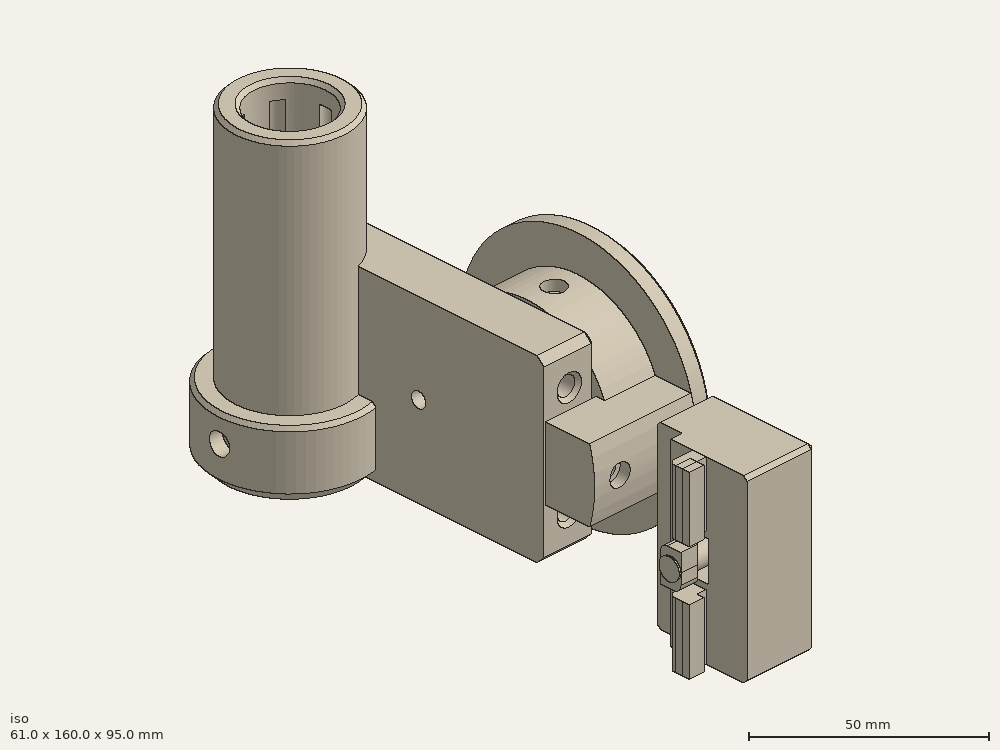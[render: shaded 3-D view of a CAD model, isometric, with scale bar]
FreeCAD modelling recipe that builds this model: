
FCSTD DOCUMENT  (FreeCAD 0.18R16146 (Git))
Label: mini-spoll-holder
License: All rights reserved
LicenseURL: http://en.wikipedia.org/wiki/All_rights_reserved
objects: Part::Cylinder×42, Part::Cut×37, Part::Box×20, Part::Chamfer×17, Part::MultiFuse×17, Part::Feature×11, Part::MultiCommon×1, Part::Fillet×1
note: 146 computed .brp shape members not serialized (recipe doc carries the construction recipe); baked Part::Feature solids carry a one-line shape summary decoded from their .brp

FEATURE [Part::Cylinder] Cylinder
  Angle = 360
  AttacherType = Attacher::AttachEngine3D
  Height = 47
  Placement = pos=(9.99127,-50,25.0035) rot=(0,1,0;1.57045rad)
  Radius = 9.65
FEATURE [Part::Box] Box003  label="Cube003"
  AttacherType = Attacher::AttachEngine3D
  Height = 50
  Length = 20
  Placement = pos=(0,-70,0) rot=(0,0,1;0rad)
  Width = 95
FEATURE [Part::Cylinder] Cylinder001
  Angle = 360
  AttacherType = Attacher::AttachEngine3D
  Height = 110
  Placement = pos=(12.5,5.00349,9.99825) rot=(1,0,0;1.57045rad)
  Radius = 2.6
FEATURE [Part::Cylinder] Cylinder002
  Angle = 360
  AttacherType = Attacher::AttachEngine3D
  Height = 110
  Placement = pos=(12.5,5.01396,39.9983) rot=(1,0,0;1.57045rad)
  Radius = 2.6
FEATURE [Part::Box] Box004  label="Cube004"
  AttacherType = Attacher::AttachEngine3D
  Height = 50
  Length = 5
  Placement = pos=(0,-70,0) rot=(0,0,1;0rad)
  Width = 70
FEATURE [Part::Chamfer] Chamfer
  Base = -> Box004
  Edges = 1 edges r=1.5: [Edge7]
FEATURE [Part::Cylinder] Cylinder003
  Angle = 360
  AttacherType = Attacher::AttachEngine3D
  Height = 27
  Placement = pos=(-3,15,-0.0010472) rot=(0,1,0;1.57045rad)
  Radius = 2.6
FEATURE [Part::Cylinder] Cylinder004
  Angle = 360
  AttacherType = Attacher::AttachEngine3D
  Height = 6
  Placement = pos=(15,15,0.00523599) rot=(0,1,0;1.57045rad)
  Radius = 6.5
FEATURE [Part::Cut] Cut
  Base = -> Box003
  Tool = -> Chamfer
FEATURE [Part::Box] Box005  label="Cube005"
  AttacherType = Attacher::AttachEngine3D
  Height = 50
  Length = 3.5
  Placement = pos=(0,19.5,0) rot=(0,0,1;0rad)
  Width = 15
FEATURE [Part::Cut] Cut001
  Base = -> Cut
  Tool = -> Box005
FEATURE [Part::Box] Box006  label="Cube006"
  AttacherType = Attacher::AttachEngine3D
  Height = 5
  Length = 2
  Placement = pos=(-2,11.9,0) rot=(0,0,1;0rad)
  Width = 6.2
FEATURE [Part::Box] Box007  label="Cube007"
  AttacherType = Attacher::AttachEngine3D
  Height = 5
  Length = 2
  Placement = pos=(-2,11.9,45) rot=(0,0,1;0rad)
  Width = 6.2
FEATURE [Part::Box] Box008  label="Cube008"
  AttacherType = Attacher::AttachEngine3D
  Height = 20
  Length = 2
  Placement = pos=(-2,11.9,15) rot=(0,0,1;0rad)
  Width = 6.2
FEATURE [Part::MultiFuse] Fusion002
  Shapes = -> [Box007,Box008,Box006,Cut001]
FEATURE [Part::MultiFuse] Fusion003
  Placement = pos=(0,0,10) rot=(0,0,1;0rad)
  Shapes = -> [Cylinder003,Cylinder004]
FEATURE [Part::Feature] Fusion003001  label="Fusion004"
  Placement = pos=(0,0,40) rot=(0,0,1;0rad)
  shape: bbox 27 x 13 x 13 mm, 7 faces (baked)
FEATURE [Part::MultiFuse] Fusion003002
  Shapes = -> [Fusion003001,Fusion003]
FEATURE [Part::Cut] Cut002
  Base = -> Fusion002
  Tool = -> Fusion003002
FEATURE [Part::Cylinder] Cylinder005
  Angle = 360
  AttacherType = Attacher::AttachEngine3D
  Height = 47
  Placement = pos=(9.99127,-50,25.0035) rot=(0,1,0;1.57045rad)
  Radius = 8.65
FEATURE [Part::Cut] Cut003
  Base = -> Cylinder
  Tool = -> Cylinder005
FEATURE [Part::Cut] Cut004
  Base = -> Cut002
  Tool = -> Cut003
FEATURE [Part::Chamfer] Chamfer001
  Base = -> Cut004
  Edges = 4 edges r=2: [Edge22,Edge24,Edge36,Edge38]
FEATURE [Part::Cylinder] Cylinder006
  Angle = 360
  AttacherType = Attacher::AttachEngine3D
  Height = 20
  Placement = pos=(24.9913,-50,25.0087) rot=(0,1,0;1.57045rad)
  Radius = 9.65
FEATURE [Part::Cylinder] Cylinder008
  Angle = 360
  AttacherType = Attacher::AttachEngine3D
  Height = 5
  Placement = pos=(39.9913,-50,25.014) rot=(0,1,0;1.57045rad)
  Radius = 35
FEATURE [Part::Cylinder] Cylinder009
  Angle = 360
  AttacherType = Attacher::AttachEngine3D
  Height = 30
  Placement = pos=(9.99127,-50,25.0035) rot=(0,1,0;1.57045rad)
  Radius = 35
FEATURE [Part::Box] Box010  label="Cube010"
  AttacherType = Attacher::AttachEngine3D
  Height = 89
  Length = 48
  Placement = pos=(0,-70.5,-13) rot=(0,0,1;0rad)
  Width = 60
FEATURE [Part::Cylinder] Cylinder007
  Angle = 360
  AttacherType = Attacher::AttachEngine3D
  Height = 20
  Placement = pos=(24.9913,-50,25.0087) rot=(0,1,0;1.57045rad)
  Radius = 25
FEATURE [Part::Box] Box011  label="Cube011"
  AttacherType = Attacher::AttachEngine3D
  Height = 20
  Length = 32
  Placement = pos=(10,-90,15) rot=(0,0,1;0rad)
  Width = 20
FEATURE [Part::Cut] Cut005
  Base = -> Cylinder009
  Tool = -> Box010
FEATURE [Part::MultiCommon] Common
  Shapes = -> [Box011,Cut005]
FEATURE [Part::MultiFuse] Fusion003003
  Shapes = -> [Cylinder007,Common,Cylinder008]
FEATURE [Part::Cut] Cut006
  Base = -> Fusion003003
  Placement = pos=(-5,0,0) rot=(0,0,1;0rad)
  Tool = -> Cylinder006
FEATURE [Part::Cylinder] Cylinder010
  Angle = 360
  AttacherType = Attacher::AttachEngine3D
  Height = 37
  Placement = pos=(12.5,-96.5087,24.9977) rot=(-1,0,0;1.57045rad)
  Radius = 1.65
FEATURE [Part::Cylinder] Cylinder011
  Angle = 360
  AttacherType = Attacher::AttachEngine3D
  Height = 37
  Placement = pos=(12.5,-90.0087,25) rot=(-1,0,0;1.57045rad)
  Radius = 1.65
FEATURE [Part::Cylinder] Cylinder012
  Angle = 360
  AttacherType = Attacher::AttachEngine3D
  Height = 37
  Placement = pos=(12.5,-119.009,24.9899) rot=(-1,0,0;1.57045rad)
  Radius = 3
FEATURE [Part::Cylinder] Cylinder013
  Angle = 360
  AttacherType = Attacher::AttachEngine3D
  Height = 37
  Placement = pos=(12.5,-100.009,24.9965) rot=(-1,0,0;1.57045rad)
  Radius = 2.1
FEATURE [Part::Cut] Cut007
  Base = -> Chamfer001
  Tool = -> Cylinder010
FEATURE [Part::Cut] Cut008
  Base = -> Cut007
  Tool = -> Cylinder013
FEATURE [Part::Cut] Cut009
  Base = -> Cut006
  Tool = -> Cylinder011
FEATURE [Part::Cut] Cut010
  Base = -> Cut009
  Tool = -> Cylinder012
FEATURE [Part::Cylinder] Cylinder014
  Angle = 360
  AttacherType = Attacher::AttachEngine3D
  Height = 11
  Placement = pos=(28,-50,47) rot=(0,0,1;0rad)
  Radius = 3
FEATURE [Part::Cylinder] Cylinder015
  Angle = 360
  AttacherType = Attacher::AttachEngine3D
  Height = 59
  Placement = pos=(28,-50,0) rot=(0,0,1;0rad)
  Radius = 1.65
FEATURE [Part::Cut] Cut011
  Base = -> Cut010
  Tool = -> Cylinder015
FEATURE [Part::Cylinder] Cylinder016
  Angle = 360
  AttacherType = Attacher::AttachEngine3D
  Height = 10
  Placement = pos=(28,-50,-7) rot=(0,0,1;0rad)
  Radius = 3
FEATURE [Part::Cylinder] Cylinder017
  Angle = 360
  AttacherType = Attacher::AttachEngine3D
  Height = 8
  Placement = pos=(34.9913,-33,25.0122) rot=(0,1,0;1.57045rad)
  Radius = 3
FEATURE [Part::Cylinder] Cylinder018
  Angle = 360
  AttacherType = Attacher::AttachEngine3D
  Height = 61
  Placement = pos=(3.99127,-33,25.0014) rot=(0,1,0;1.57045rad)
  Radius = 1.65
FEATURE [Part::Cylinder] Cylinder019
  Angle = 360
  AttacherType = Attacher::AttachEngine3D
  Height = 61
  Placement = pos=(3.99127,-33,25.0014) rot=(0,1,0;1.57045rad)
  Radius = 1.65
FEATURE [Part::Cut] Cut014
  Base = -> Cut008
  Tool = -> Cylinder018
FEATURE [Part::Cylinder] Cylinder020
  Angle = 360
  AttacherType = Attacher::AttachEngine3D
  Height = 7
  Placement = pos=(3.99127,-33,25.0014) rot=(0,1,0;1.57045rad)
  Radius = 2.1
FEATURE [Part::Cut] Cut016
  Base = -> Cut014
  Tool = -> Cylinder020
FEATURE [Part::Cylinder] Cylinder021
  Angle = 360
  AttacherType = Attacher::AttachEngine3D
  Height = 110
  Placement = pos=(12.5,5.00349,9.99825) rot=(1,0,0;1.57045rad)
  Radius = 2.6
FEATURE [Part::Cylinder] Cylinder022
  Angle = 360
  AttacherType = Attacher::AttachEngine3D
  Height = 110
  Placement = pos=(12.5,5.01396,39.9983) rot=(1,0,0;1.57045rad)
  Radius = 2.6
FEATURE [Part::MultiFuse] Fusion003004
  Shapes = -> [Cylinder001,Cylinder002]
FEATURE [Part::MultiFuse] Fusion003005
  Placement = pos=(0,-20,0) rot=(0,0,1;0rad)
  Shapes = -> [Cylinder022,Cylinder021]
FEATURE [Part::Cut] Cut018
  Base = -> Cut016
  Tool = -> Fusion003004
FEATURE [Part::Box] Box012  label="Cube012"
  AttacherType = Attacher::AttachEngine3D
  Height = 50
  Length = 20
  Placement = pos=(0,-135,0) rot=(0,0,1;0rad)
  Width = 30
FEATURE [Part::Cut] Cut019
  Base = -> Box012
  Tool = -> Fusion003005
FEATURE [Part::Box] Box013  label="Cube013"
  AttacherType = Attacher::AttachEngine3D
  Height = 50
  Length = 7
  Placement = pos=(-7,-123,0) rot=(0,0,1;0rad)
  Width = 4
FEATURE [Part::Box] Box014  label="Cube014"
  AttacherType = Attacher::AttachEngine3D
  Height = 50
  Length = 4.3
  Placement = pos=(-7,-125,0) rot=(0,0,1;0rad)
  Width = 4
FEATURE [Part::Chamfer] Chamfer005
  Base = -> Cut019
  Edges = 8 edges r=1: [Edge5,Edge6,Edge7,Edge8,Edge9,Edge10,Edge11,Edge14]
FEATURE [Part::Chamfer] Chamfer006
  Base = -> Cut018
  Edges = 8 edges r=1: [Edge4,Edge18,Edge21,Edge22,Edge23,Edge24,Edge25,Edge26]
FEATURE [Part::Box] Box015  label="Cube015"
  AttacherType = Attacher::AttachEngine3D
  Height = 50
  Length = 3.5
  Placement = pos=(0,-112.5,0) rot=(0,0,1;0rad)
  Width = 7.5
FEATURE [Part::Cut] Cut020
  Base = -> Chamfer005
  Tool = -> Box015
FEATURE [Part::Box] Box016  label="Cube016"
  AttacherType = Attacher::AttachEngine3D
  Height = 14
  Length = 20
  Placement = pos=(-12,-125,18) rot=(0,0,1;0rad)
  Width = 10
FEATURE [Part::Box] Box017  label="Cube017"
  AttacherType = Attacher::AttachEngine3D
  Height = 11
  Length = 20
  Placement = pos=(0,-123.5,19.5) rot=(0,0,1;0rad)
  Width = 7
FEATURE [Part::Cylinder] Cylinder023
  Angle = 360
  AttacherType = Attacher::AttachEngine3D
  Height = 10
  Placement = pos=(12.9913,-120,25.0045) rot=(0,1,0;1.57045rad)
  Radius = 8
FEATURE [Part::Cut] Cut021
  Base = -> Cut020
  Tool = -> Box017
FEATURE [Part::Cut] Cut022
  Base = -> Cut021
  Tool = -> Cylinder023
FEATURE [Part::Chamfer] Chamfer007
  Base = -> Cut022
  Edges = 2 edges r=0.4: [Edge28,Edge32]
FEATURE [Part::Chamfer] Chamfer008
  Base = -> Chamfer007
  Edges = 1 edges r=1: [Edge46]
FEATURE [Part::Box] Box019  label="Cube019"
  AttacherType = Attacher::AttachEngine3D
  Height = 10
  Length = 5
  Placement = pos=(-7.5,-123,20) rot=(0,0,1;0rad)
  Width = 6
FEATURE [Part::Cylinder] Cylinder024
  Angle = 360
  AttacherType = Attacher::AttachEngine3D
  Height = 27
  Placement = pos=(-8.00873,-120,24.9972) rot=(0,1,0;1.57045rad)
  Radius = 3
FEATURE [Part::Fillet] Fillet
  Base = -> Box019
  Edges = 2 edges r=2: [Edge9,Edge12]
FEATURE [Part::Box] Box020  label="Cube020"
  AttacherType = Attacher::AttachEngine3D
  Height = 7
  Length = 7
  Placement = pos=(15,-121,21.5) rot=(0,0,1;0rad)
  Width = 2
FEATURE [Part::Cylinder] Cylinder025
  Angle = 360
  AttacherType = Attacher::AttachEngine3D
  Height = 7
  Placement = pos=(12.9913,-120,25.0045) rot=(0,1,0;1.57045rad)
  Radius = 7
FEATURE [Part::MultiFuse] Fusion003009
  Shapes = -> [Cylinder025,Fillet,Cylinder024]
FEATURE [Part::Chamfer] Chamfer012
  Base = -> Chamfer006
  Edges = 2 edges r=1: [Edge75,Edge77]
FEATURE [Part::Cylinder] Cylinder026
  Angle = 360
  AttacherType = Attacher::AttachEngine3D
  Height = 37
  Placement = pos=(-6e-15,-50,25) rot=(0,1,0;1.5708rad)
  Radius = 9.6
FEATURE [Part::Cylinder] Cylinder027
  Angle = 360
  AttacherType = Attacher::AttachEngine3D
  Height = 37
  Placement = pos=(-6e-15,-50,25) rot=(0,1,0;1.5708rad)
  Radius = 8.15
FEATURE [Part::Cut] Cut026
  Base = -> Cylinder026
  Placement = pos=(10,0,0) rot=(0,0,1;0rad)
  Tool = -> Cylinder027
FEATURE [Part::Cut] Cut027
  Base = -> Chamfer012
  Tool = -> Cut026
FEATURE [Part::Chamfer] Chamfer013  label="spool-top"
  Base = -> Cut027
  Edges = 2 edges r=1: [Edge49,Edge138]
FEATURE [Part::Cut] Cut028
  Base = -> Cut011
  Tool = -> Cylinder019
FEATURE [Part::Cut] Cut029
  Base = -> Cut028
  Tool = -> Cylinder017
FEATURE [Part::Cylinder] Cylinder028
  Angle = 360
  AttacherType = Attacher::AttachEngine3D
  Height = 11
  Placement = pos=(28,-50,40) rot=(0,0,1;0rad)
  Radius = 2.1
FEATURE [Part::Cylinder] Cylinder029
  Angle = 360
  AttacherType = Attacher::AttachEngine3D
  Height = 10
  Placement = pos=(28,-50,0) rot=(0,0,1;0rad)
  Radius = 2.1
FEATURE [Part::Cut] Cut030
  Base = -> Cut029
  Tool = -> Cylinder029
FEATURE [Part::Cut] Cut031
  Base = -> Cut030
  Tool = -> Cylinder028
FEATURE [Part::Cut] Cut032
  Base = -> Cut031
  Tool = -> Cylinder014
FEATURE [Part::Cut] Cut033
  Base = -> Cut032
  Tool = -> Cylinder016
FEATURE [Part::Chamfer] Chamfer014
  Base = -> Cut033
  Edges = 2 edges r=1: [Edge3,Edge4]
FEATURE [Part::Chamfer] Chamfer015  label="spool-side"
  Base = -> Chamfer014
  Edges = 1 edges r=0.4: [Edge3]
FEATURE [Part::Cut] Cut034
  Base = -> Fusion003009
  Tool = -> Box020
FEATURE [Part::Chamfer] Chamfer016  label="lock"
  Base = -> Cut034
  Edges = 5 edges r=0.4: [Edge1,Edge4,Edge5,Edge6,Edge7]
FEATURE [Part::Chamfer] Chamfer017
  Base = -> Box013
  Edges = 1 edges r=1: [Edge3]
FEATURE [Part::MultiFuse] Fusion
  Shapes = -> [Chamfer017,Box014]
FEATURE [Part::Cut] Cut035
  Base = -> Fusion
  Tool = -> Box016
FEATURE [Part::MultiFuse] Fusion003010
  Shapes = -> [Chamfer008,Cut035]
FEATURE [Part::Chamfer] Chamfer018  label="spool-bottom"
  Base = -> Fusion003010
  Edges = 2 edges r=1: [Edge77,Edge78]
FEATURE [Part::Cylinder] Cylinder035007  label="Cylinder042"
  Angle = 360
  AttacherType = Attacher::AttachEngine3D
  Height = 101
  Placement = pos=(0,0,-4) rot=(0,0,1;0rad)
  Radius = 10.5
FEATURE [Part::Cylinder] Cylinder035008  label="Cylinder043"
  Angle = 360
  AttacherType = Attacher::AttachEngine3D
  Height = 85
  Radius = 16
FEATURE [Part::Cylinder] Cylinder035009  label="Cylinder044"
  Angle = 360
  AttacherType = Attacher::AttachEngine3D
  Height = 10
  Placement = pos=(0,11.75,0) rot=(0,0,1;0rad)
  Radius = 2.25
FEATURE [Part::Feature] Cylinder035009001  label="Cylinder045"
  Placement = pos=(0,0,0) rot=(0,0,1;5.23599rad)
  shape: bbox 4.5 x 4.5 x 10 mm, 3 faces (baked)
FEATURE [Part::Feature] Cylinder035009002  label="Cylinder046"
  Placement = pos=(0,0,0) rot=(0,0,1;4.18879rad)
  shape: bbox 4.5 x 4.5 x 10 mm, 3 faces (baked)
FEATURE [Part::Feature] Cylinder035009003  label="Cylinder047"
  Placement = pos=(0,0,0) rot=(0,0,-1;3.14159rad)
  shape: bbox 4.5 x 4.5 x 10 mm, 3 faces (baked)
FEATURE [Part::Feature] Cylinder035009004  label="Cylinder048"
  Placement = pos=(0,0,0) rot=(0,0,-1;4.18879rad)
  shape: bbox 4.5 x 4.5 x 10 mm, 3 faces (baked)
FEATURE [Part::Feature] Cylinder035009005  label="Cylinder049"
  Placement = pos=(0,0,0) rot=(0,0,-1;5.23599rad)
  shape: bbox 4.5 x 4.5 x 10 mm, 3 faces (baked)
FEATURE [Part::MultiFuse] Fusion003012
  Shapes = -> [Cylinder035009005,Cylinder035009004,Cylinder035009003,Cylinder035009002,Cylinder035009001,Cylinder035009]
FEATURE [Part::Feature] Fusion003012001  label="Fusion003013"
  Placement = pos=(0,0,1) rot=(0,0,1;0rad)
  shape: bbox 24.85 x 28 x 10 mm, 18 faces, 6 solids (baked)
FEATURE [Part::MultiFuse] Fusion003012002
  Placement = pos=(0,0,5) rot=(0,0,1;0rad)
  Shapes = -> [Fusion003012001,Fusion003012]
FEATURE [Part::Feature] Fusion003012002002  label="Fusion003012004"
  Placement = pos=(0,0,19) rot=(0,0,1;0.523599rad)
  shape: bbox 28 x 24.85 x 11 mm, 30 faces, 6 solids (baked)
FEATURE [Part::Feature] Fusion003012002003  label="Fusion003012005"
  Placement = pos=(0,0,74) rot=(0,0,1;0.523599rad)
  shape: bbox 28 x 24.85 x 11 mm, 30 faces, 6 solids (baked)
FEATURE [Part::Feature] Fusion003012002004  label="Fusion003012006"
  Placement = pos=(0,0,60) rot=(0,0,1;0rad)
  shape: bbox 24.85 x 28 x 11 mm, 30 faces, 6 solids (baked)
FEATURE [Part::MultiFuse] Fusion003012002005
  Placement = pos=(0,0,-5) rot=(0,0,1;0rad)
  Shapes = -> [Fusion003012002003,Fusion003012002004]
FEATURE [Part::MultiFuse] Fusion003012002006
  Shapes = -> [Fusion003012002,Fusion003012002002]
FEATURE [Part::MultiFuse] Fusion003012002007
  Shapes = -> [Fusion003012002005,Fusion003012002006]
FEATURE [Part::Cylinder] Cylinder035009007  label="Cylinder051"
  Angle = 360
  AttacherType = Attacher::AttachEngine3D
  Height = 20
  Placement = pos=(0,0,4) rot=(0,0,1;0rad)
  Radius = 9.75
FEATURE [Part::Cylinder] Cylinder035009008  label="Cylinder052"
  Angle = 360
  AttacherType = Attacher::AttachEngine3D
  Height = 19
  Radius = 21
FEATURE [Part::Cut] Cut039
  Base = -> Cylinder035008
  Tool = -> Cylinder035007
FEATURE [Part::Cut] Cut040
  Base = -> Cut039
  Tool = -> Fusion003012002007
FEATURE [Part::Chamfer] Chamfer019  label="roller"
  Base = -> Cut040
  Edges = 4 edges r=1: [Edge1,Edge3,Edge4,Edge5]
FEATURE [Part::Cylinder] Cylinder035009009  label="Cylinder053"
  Angle = 360
  AttacherType = Attacher::AttachEngine3D
  Height = 35
  Placement = pos=(-17,0,12) rot=(0,1,0;4.71239rad)
  Radius = 3
FEATURE [Part::Cylinder] Cylinder035009010  label="Cylinder054"
  Angle = 360
  AttacherType = Attacher::AttachEngine3D
  Height = 35
  Placement = pos=(17,0,12) rot=(0,1,0;1.5708rad)
  Radius = 3
FEATURE [Part::Cylinder] Cylinder035009011  label="Cylinder055"
  Angle = 360
  AttacherType = Attacher::AttachEngine3D
  Height = 35
  Placement = pos=(-3e-15,0,12) rot=(0,1,0;1.5708rad)
  Radius = 1.65
FEATURE [Part::Cylinder] Cylinder035009012  label="Cylinder056"
  Angle = 360
  AttacherType = Attacher::AttachEngine3D
  Height = 35
  Placement = pos=(-3e-15,0,12) rot=(0,-1,0;1.5708rad)
  Radius = 1.65
FEATURE [Part::MultiFuse] Fusion003012002008
  Shapes = -> [Cylinder035009012,Cylinder035009011]
FEATURE [Part::Cylinder] Cylinder035009013  label="Cylinder057"
  Angle = 360
  AttacherType = Attacher::AttachEngine3D
  Height = 35
  Placement = pos=(11,0,12) rot=(0,1,0;1.5708rad)
  Radius = 2.1
FEATURE [Part::Cylinder] Cylinder035009014  label="Cylinder058"
  Angle = 360
  AttacherType = Attacher::AttachEngine3D
  Height = 35
  Placement = pos=(-11,0,12) rot=(0,-1,0;1.5708rad)
  Radius = 2.1
FEATURE [Part::MultiFuse] Fusion003012002009
  Shapes = -> [Cylinder035009014,Cylinder035009013]
FEATURE [Part::Box] Box  label="Cube"
  AttacherType = Attacher::AttachEngine3D
  Height = 10
  Length = 20
  Placement = pos=(0,-2.1,3) rot=(0,0,1;0rad)
  Width = 4.2
FEATURE [Part::Box] Box021  label="Cube021"
  AttacherType = Attacher::AttachEngine3D
  Height = 9
  Length = 20
  Placement = pos=(0,-5,0) rot=(0,0,1;0rad)
  Width = 10
FEATURE [Part::Cut] Cut046
  Base = -> Box021
  Tool = -> Box
FEATURE [Part::Box] Box022  label="Cube022"
  AttacherType = Attacher::AttachEngine3D
  Height = 10
  Length = 1
  Placement = pos=(9.5,-5,3) rot=(0,0,1;0rad)
  Width = 10
FEATURE [Part::Cut] Cut047
  Base = -> Cut046
  Tool = -> Box022
FEATURE [Part::Box] Box023  label="Cube023"
  AttacherType = Attacher::AttachEngine3D
  Height = 10
  Length = 10
  Placement = pos=(0,-5,8) rot=(0,0,1;0rad)
  Width = 10
FEATURE [Part::Cut] Cut048
  Base = -> Cut047
  Tool = -> Box023
FEATURE [Part::Feature] Cut048001  label="Cut049"
  shape: bbox 20 x 10 x 9 mm, 18 faces (baked)
FEATURE [Part::Cylinder] Cylinder035009015  label="Cylinder059"
  Angle = 360
  AttacherType = Attacher::AttachEngine3D
  Height = 10
  Placement = pos=(0,5,10) rot=(1,0,0;1.5708rad)
  Radius = 7
FEATURE [Part::Cut] Cut048002
  Base = -> Cut048001
  Tool = -> Cylinder035009015
FEATURE [Part::Chamfer] Chamfer022
  Base = -> Cut048002
  Edges = 25 edges r=0.4: [Edge4,Edge5,Edge6,Edge16,Edge26,Edge27,Edge28,Edge29,Edge30,Edge31,Edge34,Edge35,Edge36,Edge37,Edge38,Edge41,Edge42,Edge44,Edge45,Edge46,Edge47,Edge48,Edge49,Edge51,Edge52]
FEATURE [Part::Cut] Cut048003
  Base = -> Cylinder035009008
  Tool = -> Cylinder035009007
FEATURE [Part::MultiFuse] Fusion003012002010
  Placement = pos=(0,0,-0.5) rot=(0,0,1;0rad)
  Shapes = -> [Cylinder035009010,Cylinder035009009,Fusion003012002009,Fusion003012002008]
FEATURE [Part::Cut] Cut048004
  Base = -> Cut048003
  Tool = -> Fusion003012002010
FEATURE [Part::Chamfer] Chamfer023
  Base = -> Cut048004
  Edges = 1 edges r=3: [Edge4]
FEATURE [Part::Chamfer] Chamfer024
  Base = -> Chamfer023
  Edges = 2 edges r=1: [Edge6,Edge12]
